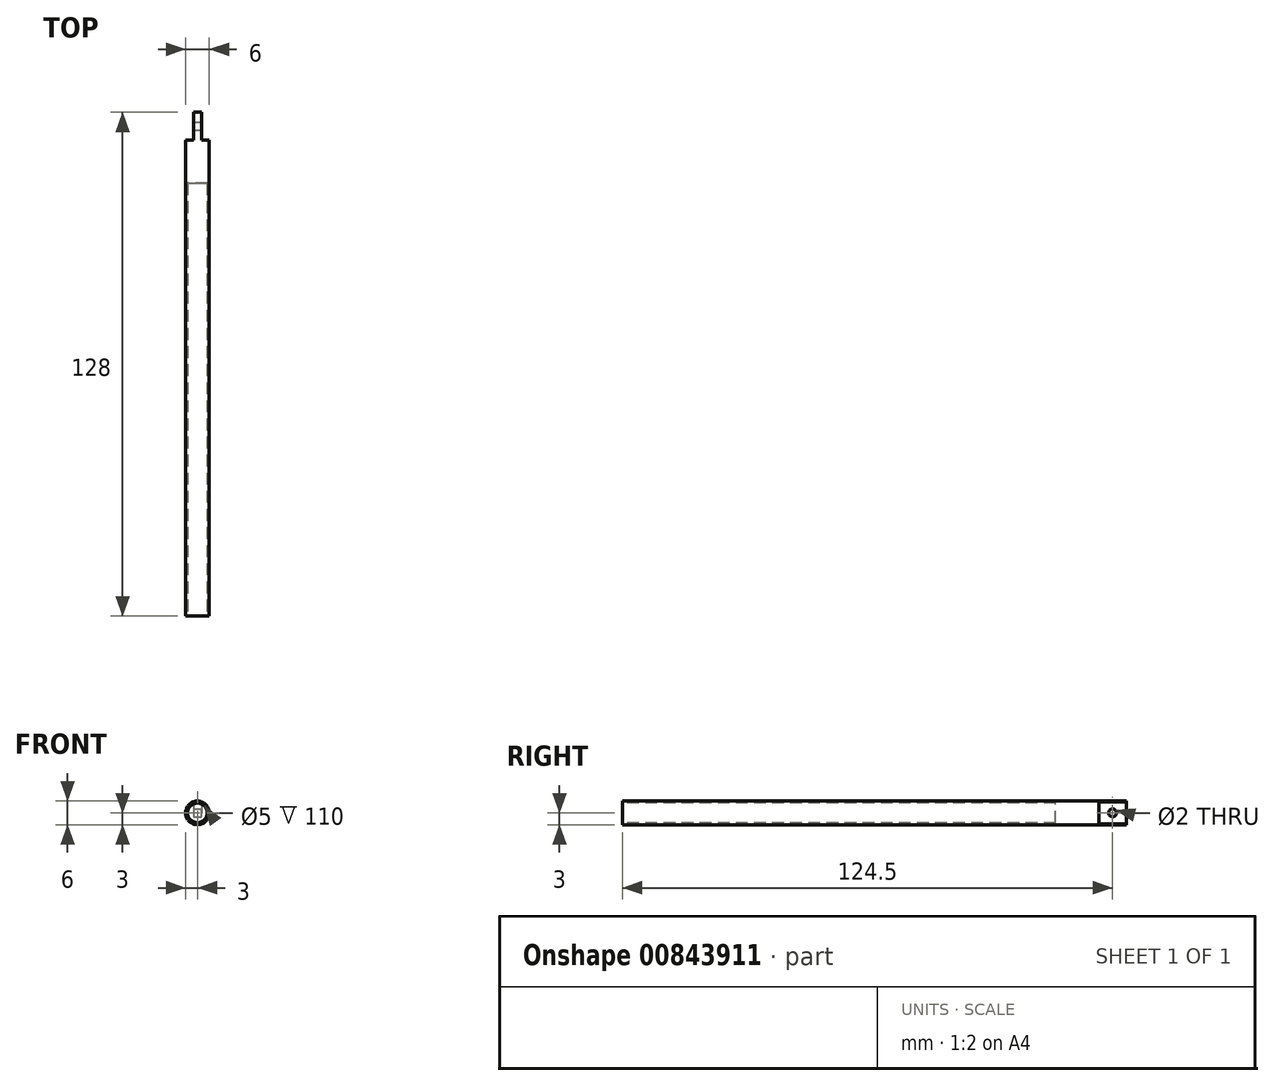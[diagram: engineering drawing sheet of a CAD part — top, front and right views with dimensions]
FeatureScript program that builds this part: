
annotation { "Feature Type Name" : "Feature", "Feature Type Description" : "" }
export const myFeature = defineFeature(function(context is Context, id is Id, definition is map)
    precondition{}
    {
        {
            var Q0;
            Q0=qCreatedBy(makeId("Front.planeOp"),FACE);
            var sketch = newSketch(context, id + "F0", { "sketchPlane" : qUnion([Q0])});
            skCircle(sketch, "E0", {"center": v(0, 0) * mm, "radius": 3 * mm});
            skSolve(sketch);
        }
        {
            var Q0;
            Q0 = qSketchRegion(id + "F0", true);
            extrude(context, id + "F1", {"entities" : qUnion([Q0]), "endBound" : BoundingType.SYMMETRIC, "depth" : 128 * mm, "offsetDistance" : 25 * mm});
        }
        {
            var Q0;
            Q0=qCreatedBy(makeId("Top.planeOp"),FACE);
            var sketch = newSketch(context, id + "F2", { "sketchPlane" : qUnion([Q0])});
            skLineSegment(sketch, "E1.bottom", {"start": v(-1, 67) * mm, "end": v(-5.4, 67) * mm});
            skLineSegment(sketch, "E1.top", {"start": v(-1, 57) * mm, "end": v(-5.4, 57) * mm});
            skLineSegment(sketch, "E1.left", {"start": v(-1, 67) * mm, "end": v(-1, 57) * mm});
            skLineSegment(sketch, "E1.right", {"start": v(-5.4, 67) * mm, "end": v(-5.4, 57) * mm});
            skLineSegment(sketch, "E2.bottom", {"start": v(1, 67) * mm, "end": v(5.7, 67) * mm});
            skLineSegment(sketch, "E2.top", {"start": v(1, 57) * mm, "end": v(5.7, 57) * mm});
            skLineSegment(sketch, "E2.left", {"start": v(1, 67) * mm, "end": v(1, 57) * mm});
            skLineSegment(sketch, "E2.right", {"start": v(5.7, 67) * mm, "end": v(5.7, 57) * mm});
            skSolve(sketch);
        }
        {
            var Q0;
            Q0 = qSketchRegion(id + "F2", true);
            extrude(context, id + "F3", {"entities" : qUnion([Q0]), "operationType" : NewBodyOperationType.REMOVE, "endBound" : BoundingType.SYMMETRIC, "oppositeDirection" : true, "depth" : 68 * mm, "offsetDistance" : 25 * mm});
        }
        {
            var Q0;
            Q0=makeQuery(id+"F3.boolean.opBoolean","COPY",FACE,{"derivedFrom":makeQuery(id+"F3.opExtrude","SWEPT_FACE",FACE,{"disambiguationData":[OSD([sQuery(id+"F2.wireOp",EDGE,"E2.left")])]})});
            var sketch = newSketch(context, id + "F4", { "sketchPlane" : qUnion([Q0])});
            skLineSegment(sketch, "E3", {"start": v(64, 0) * mm, "end": v(57, 0) * mm, "construction": true});
            skCircle(sketch, "E4", {"center": v(60.5, 0) * mm, "radius": 1 * mm});
            skSolve(sketch);
        }
        {
            var Q0;
            Q0 = qSketchRegion(id + "F4", true);
            extrude(context, id + "F5", {"entities" : qUnion([Q0]), "operationType" : NewBodyOperationType.REMOVE, "oppositeDirection" : true, "depth" : 25.4 * mm, "offsetDistance" : 25 * mm});
        }
        {
            var Q0;
            Q0=makeQuery(id+"F1.opExtrude","CAP_FACE",FACE,{"disambiguationData":[OSD([sQuery(id+"F0.wireOp",EDGE,"E0")])],"isStart":false});
            var sketch = newSketch(context, id + "F6", { "sketchPlane" : qUnion([Q0])});
            skCircle(sketch, "E5", {"center": v(0, 0) * mm, "radius": 2.5 * mm});
            skSolve(sketch);
        }
        {
            var Q0;
            Q0 = qSketchRegion(id + "F6", true);
            extrude(context, id + "F7", {"entities" : qUnion([Q0]), "operationType" : NewBodyOperationType.REMOVE, "oppositeDirection" : true, "depth" : 110 * mm, "offsetDistance" : 25 * mm});
        }
    });
